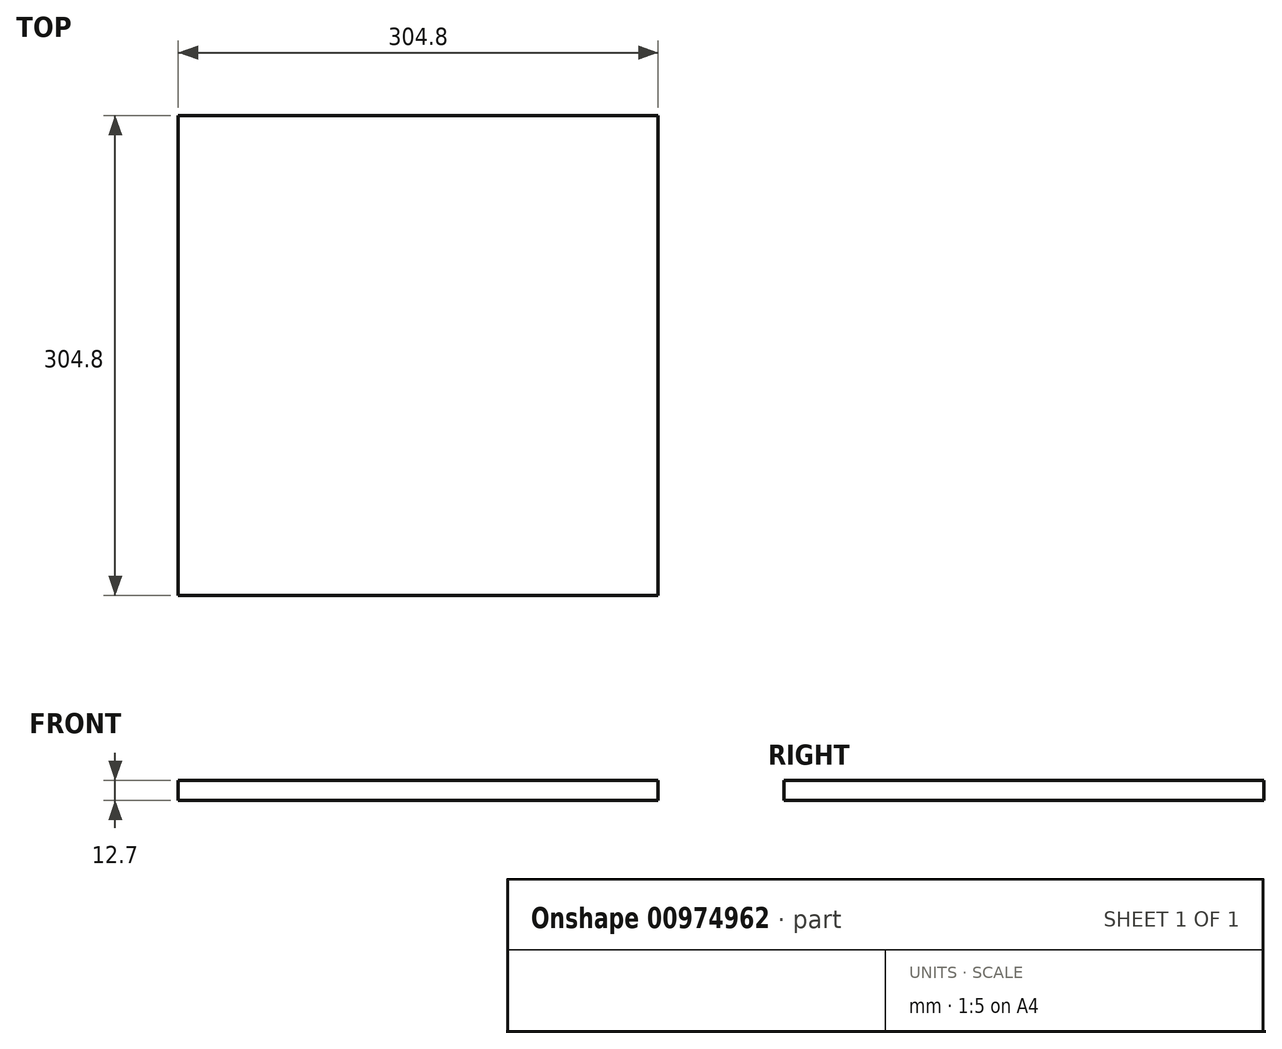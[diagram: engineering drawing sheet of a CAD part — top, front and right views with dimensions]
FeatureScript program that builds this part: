
annotation { "Feature Type Name" : "Feature", "Feature Type Description" : "" }
export const myFeature = defineFeature(function(context is Context, id is Id, definition is map)
    precondition{}
    {
        {
            var Q0;
            Q0=qCreatedBy(makeId("Top.planeOp"),FACE);
            var sketch = newSketch(context, id + "F0", { "sketchPlane" : qUnion([Q0])});
            skLineSegment(sketch, "E0.bottom", {"start": v(-151.2, 156.82) * mm, "end": v(153.6, 156.82) * mm});
            skLineSegment(sketch, "E0.top", {"start": v(-151.2, -147.98) * mm, "end": v(153.6, -147.98) * mm});
            skLineSegment(sketch, "E0.left", {"start": v(-151.2, 156.82) * mm, "end": v(-151.2, -147.98) * mm});
            skLineSegment(sketch, "E0.right", {"start": v(153.6, 156.82) * mm, "end": v(153.6, -147.98) * mm});
            skSolve(sketch);
        }
        {
            var Q0;
            Q0=makeQuery(id+"F0.imprint","IMPRINT",FACE,{"disambiguationData":[TD([[makeQuery(id+"F0.imprint","IMPRINT",EDGE,{"derivedFrom":sQuery(id+"F0.wireOp",EDGE,"E0.bottom")}),-1.0]])]});
            extrude(context, id + "F1", {"entities" : qUnion([Q0]), "depth" : 12.7 * mm, "offsetDistance" : 25.4 * mm});
        }
    });
